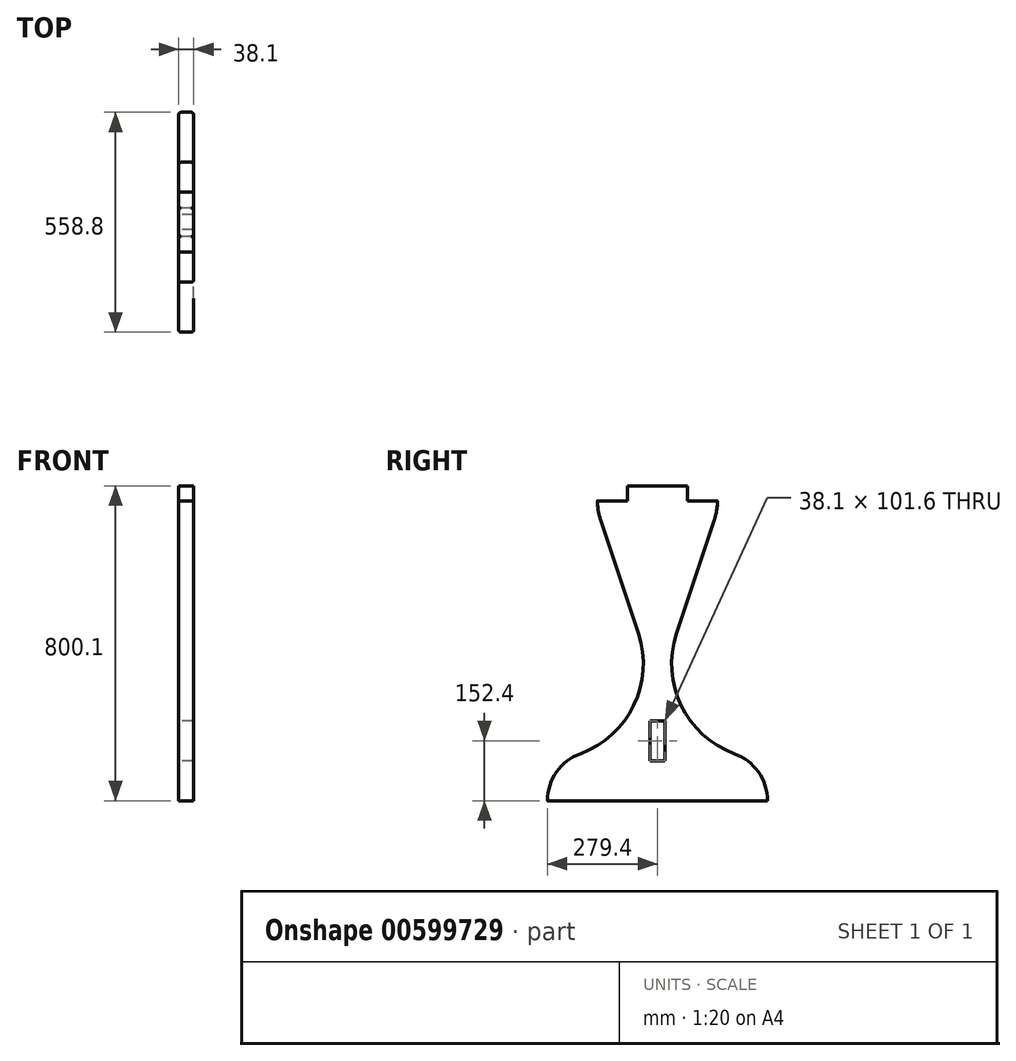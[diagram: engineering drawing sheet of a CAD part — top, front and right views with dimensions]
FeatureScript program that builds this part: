
annotation { "Feature Type Name" : "Feature", "Feature Type Description" : "" }
export const myFeature = defineFeature(function(context is Context, id is Id, definition is map)
    precondition{}
    {
        {
            var Q0;
            Q0=qCreatedBy(makeId("Right.planeOp"),FACE);
            var sketch = newSketch(context, id + "F0", { "sketchPlane" : qUnion([Q0])});
            skLineSegment(sketch, "E0", {"start": v(0, 0) * mm, "end": v(0, 762) * mm, "construction": true});
            skLineSegment(sketch, "E1", {"start": v(0, 0) * mm, "end": v(-279.4, 0) * mm});
            skArc(sketch, "E2", {"start": v(-195.95, 119.3) * mm, "mid": v(-60.25, 242.07) * mm, "end": v(-48.46, 424.69) * mm});
            skArc(sketch, "E3", {"start": v(-152.4, 762) * mm, "mid": v(-150.44, 737.65) * mm, "end": v(-144.62, 713.92) * mm});
            skLineSegment(sketch, "E4", {"start": v(-152.4, 762) * mm, "end": v(0, 762) * mm});
            skLineSegment(sketch, "E5", {"start": v(-48.46, 424.69) * mm, "end": v(-144.62, 713.92) * mm});
            skArc(sketch, "E6", {"start": v(-195.95, 119.3) * mm, "mid": v(-256.47, 72.8) * mm, "end": v(-279.4, 0) * mm});
            skArc(sketch, "E7.MirrorCS", {"start": v(195.95, 119.3) * mm, "mid": v(256.47, 72.8) * mm, "end": v(279.4, 0) * mm});
            skArc(sketch, "E8.MirrorCS", {"start": v(195.95, 119.3) * mm, "mid": v(60.25, 242.07) * mm, "end": v(48.46, 424.69) * mm});
            skLineSegment(sketch, "E9.MirrorCS", {"start": v(48.46, 424.69) * mm, "end": v(144.62, 713.92) * mm});
            skLineSegment(sketch, "E10.MirrorCS", {"start": v(152.4, 762) * mm, "end": v(0, 762) * mm});
            skLineSegment(sketch, "E11.MirrorCS", {"start": v(0, 0) * mm, "end": v(279.4, 0) * mm});
            skArc(sketch, "E12.MirrorCS", {"start": v(152.4, 762) * mm, "mid": v(150.44, 737.65) * mm, "end": v(144.62, 713.92) * mm});
            skLineSegment(sketch, "E13.bottom", {"start": v(76.2, 762) * mm, "end": v(-76.2, 762) * mm});
            skLineSegment(sketch, "E13.top", {"start": v(76.2, 800.1) * mm, "end": v(-76.2, 800.1) * mm});
            skLineSegment(sketch, "E13.left", {"start": v(76.2, 762) * mm, "end": v(76.2, 800.1) * mm});
            skLineSegment(sketch, "E13.right", {"start": v(-76.2, 762) * mm, "end": v(-76.2, 800.1) * mm});
            skSolve(sketch);
        }
        {
            var Q0;
            Q0 = qSketchRegion(id + "F0", true);
            extrude(context, id + "F1", {"entities" : qUnion([Q0]), "depth" : 38.1 * mm, "offsetDistance" : 25.4 * mm});
        }
        {
            var Q0;
            Q0=makeQuery(id+"F1.opExtrude","CAP_EDGE",EDGE,{"disambiguationData":[OSD([sQuery(id+"F0.wireOp",EDGE,"E2")])],"isStart":false});
            var Q1;
            Q1=makeQuery(id+"F1.opExtrude","CAP_EDGE",EDGE,{"disambiguationData":[OSD([sQuery(id+"F0.wireOp",EDGE,"E8.MirrorCS")])],"isStart":true});
            var Q2;
            Q2=makeQuery(id+"F1.opExtrude","CAP_EDGE",EDGE,{"disambiguationData":[OSD([sQuery(id+"F0.wireOp",EDGE,"E8.MirrorCS")])],"isStart":false});
            var Q3;
            Q3=makeQuery(id+"F1.opExtrude","CAP_EDGE",EDGE,{"disambiguationData":[OSD([sQuery(id+"F0.wireOp",EDGE,"E5")])],"isStart":true});
            fillet(context, id + "F2", {"entities" : qUnion([Q0, Q1, Q2, Q3]), "radius" : 6.35 * mm, "tangentPropagation" : true, "allowEdgeOverflow" : false});
        }
        {
            var Q0;
            Q0=makeQuery(id+"F1.opExtrude","CAP_FACE",FACE,{"disambiguationData":[OSD([sQuery(id+"F0.wireOp",EDGE,"E1"),sQuery(id+"F0.wireOp",EDGE,"E2"),sQuery(id+"F0.wireOp",EDGE,"E3"),sQuery(id+"F0.wireOp",EDGE,"E4"),sQuery(id+"F0.wireOp",EDGE,"E5"),sQuery(id+"F0.wireOp",EDGE,"E6"),sQuery(id+"F0.wireOp",EDGE,"E7.MirrorCS"),sQuery(id+"F0.wireOp",EDGE,"E8.MirrorCS"),sQuery(id+"F0.wireOp",EDGE,"E9.MirrorCS"),sQuery(id+"F0.wireOp",EDGE,"E10.MirrorCS"),sQuery(id+"F0.wireOp",EDGE,"E11.MirrorCS"),sQuery(id+"F0.wireOp",EDGE,"E12.MirrorCS")])],"isStart":true});
            var sketch = newSketch(context, id + "F3", { "sketchPlane" : qUnion([Q0])});
            skLineSegment(sketch, "E14.bottom", {"start": v(-19.05, 203.2) * mm, "end": v(19.05, 203.2) * mm});
            skLineSegment(sketch, "E14.top", {"start": v(-19.05, 101.6) * mm, "end": v(19.05, 101.6) * mm});
            skLineSegment(sketch, "E14.left", {"start": v(-19.05, 203.2) * mm, "end": v(-19.05, 101.6) * mm});
            skLineSegment(sketch, "E14.right", {"start": v(19.05, 203.2) * mm, "end": v(19.05, 101.6) * mm});
            skSolve(sketch);
        }
        {
            var Q0;
            Q0=makeQuery(id+"F3.imprint","IMPRINT",FACE,{"disambiguationData":[TD([[makeQuery(id+"F3.imprint","IMPRINT",EDGE,{"derivedFrom":sQuery(id+"F3.wireOp",EDGE,"E14.bottom")}),-1.0]])]});
            extrude(context, id + "F4", {"entities" : qUnion([Q0]), "operationType" : NewBodyOperationType.REMOVE, "endBound" : BoundingType.UP_TO_NEXT, "oppositeDirection" : true, "depth" : 25.4 * mm, "offsetDistance" : 25.4 * mm});
        }
    });
